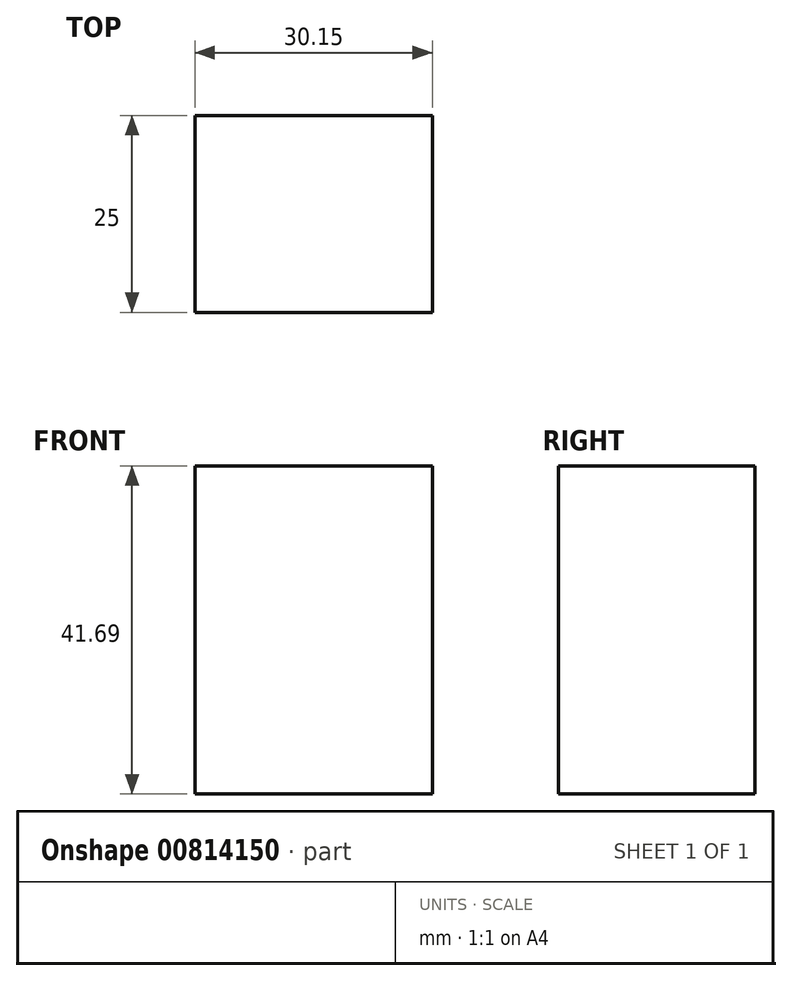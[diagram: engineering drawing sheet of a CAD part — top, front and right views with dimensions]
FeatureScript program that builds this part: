
annotation { "Feature Type Name" : "Feature", "Feature Type Description" : "" }
export const myFeature = defineFeature(function(context is Context, id is Id, definition is map)
    precondition{}
    {
        {
            var Q0;
            Q0=qCreatedBy(makeId("Front.planeOp"),FACE);
            var sketch = newSketch(context, id + "F0", { "sketchPlane" : qUnion([Q0])});
            skLineSegment(sketch, "E0.bottom", {"start": v(-65.7, 48.45) * mm, "end": v(-35.54, 48.45) * mm});
            skLineSegment(sketch, "E0.top", {"start": v(-65.7, 6.76) * mm, "end": v(-35.54, 6.76) * mm});
            skLineSegment(sketch, "E0.left", {"start": v(-65.7, 48.45) * mm, "end": v(-65.7, 6.76) * mm});
            skLineSegment(sketch, "E0.right", {"start": v(-35.54, 48.45) * mm, "end": v(-35.54, 6.76) * mm});
            skSolve(sketch);
        }
        {
            var Q0;
            Q0=makeQuery(id+"F0.imprint","IMPRINT",FACE,{"disambiguationData":[TD([[makeQuery(id+"F0.imprint","IMPRINT",EDGE,{"derivedFrom":sQuery(id+"F0.wireOp",EDGE,"E0.bottom")}),-1.0]])]});
            extrude(context, id + "F1", {"entities" : qUnion([Q0]), "depth" : 25 * mm, "offsetDistance" : 25 * mm});
        }
    });
